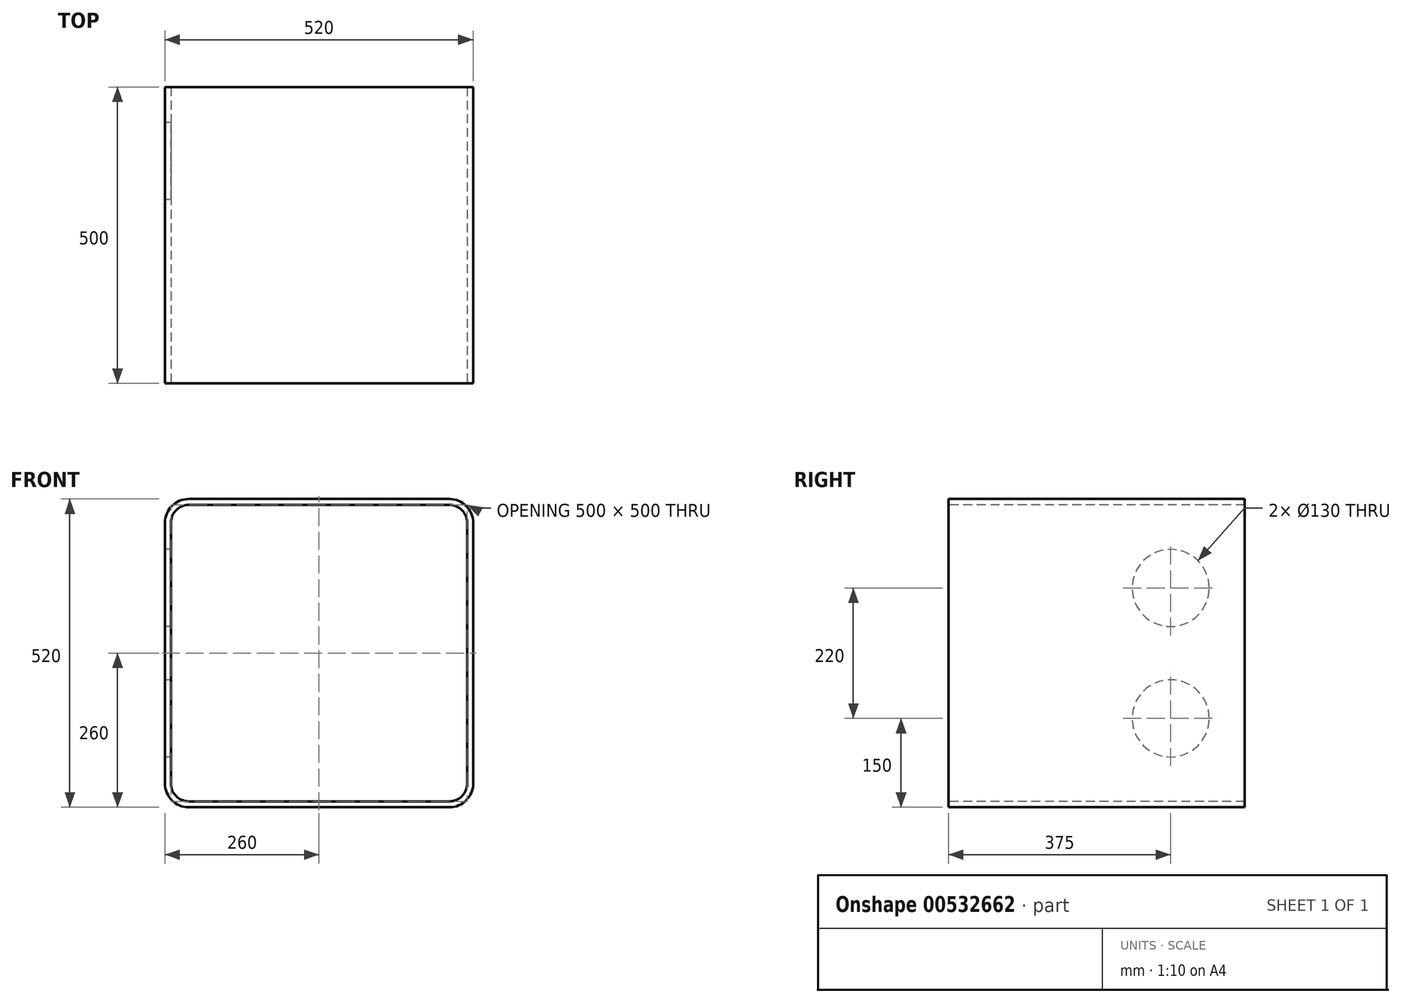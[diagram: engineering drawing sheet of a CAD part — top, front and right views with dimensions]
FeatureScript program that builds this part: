
annotation { "Feature Type Name" : "Feature", "Feature Type Description" : "" }
export const myFeature = defineFeature(function(context is Context, id is Id, definition is map)
    precondition{}
    {
        {
            var Q0;
            Q0=qCreatedBy(makeId("Front.planeOp"),FACE);
            var sketch = newSketch(context, id + "F0", { "sketchPlane" : qUnion([Q0])});
            skLineSegment(sketch, "E0.bottom", {"start": v(-215, 250) * mm, "end": v(225, 250) * mm});
            skLineSegment(sketch, "E0.top", {"start": v(-215, -250) * mm, "end": v(225, -250) * mm});
            skLineSegment(sketch, "E0.left", {"start": v(-245, 220) * mm, "end": v(-245, -220) * mm});
            skLineSegment(sketch, "E0.right", {"start": v(255, 220) * mm, "end": v(255, -220) * mm});
            skPoint(sketch, "E0.middle", {"position": v(0, 0) * mm});
            skPoint(sketch, "E1.visualSharp", {"position": v(-245, 250) * mm});
            skArc(sketch, "E1.filletArc", {"start": v(-215, 250) * mm, "mid": v(-236.21, 241.21) * mm, "end": v(-245, 220) * mm});
            skArc(sketch, "E2.filletArc", {"start": v(255, 220) * mm, "mid": v(246.21, 241.21) * mm, "end": v(225, 250) * mm});
            skArc(sketch, "E3.filletArc", {"start": v(225, -250) * mm, "mid": v(246.21, -241.21) * mm, "end": v(255, -220) * mm});
            skArc(sketch, "E4.filletArc", {"start": v(-245, -220) * mm, "mid": v(-236.21, -241.21) * mm, "end": v(-215, -250) * mm});
            skArc(sketch, "E5.0", {"start": v(-215, 260) * mm, "mid": v(-243.28, 248.28) * mm, "end": v(-255, 220) * mm});
            skLineSegment(sketch, "E5.1", {"start": v(-215, 260) * mm, "end": v(225, 260) * mm});
            skLineSegment(sketch, "E5.2", {"start": v(-255, 220) * mm, "end": v(-255, -220) * mm});
            skArc(sketch, "E5.3", {"start": v(265, 220) * mm, "mid": v(253.28, 248.28) * mm, "end": v(225, 260) * mm});
            skArc(sketch, "E5.4", {"start": v(-255, -220) * mm, "mid": v(-243.28, -248.28) * mm, "end": v(-215, -260) * mm});
            skLineSegment(sketch, "E5.5", {"start": v(-215, -260) * mm, "end": v(225, -260) * mm});
            skArc(sketch, "E5.6", {"start": v(225, -260) * mm, "mid": v(253.28, -248.28) * mm, "end": v(265, -220) * mm});
            skLineSegment(sketch, "E5.7", {"start": v(265, 220) * mm, "end": v(265, -220) * mm});
            skSolve(sketch);
        }
        {
            var Q0;
            Q0 = qSketchRegion(id + "F0", true);
            extrude(context, id + "F1", {"entities" : qUnion([Q0]), "oppositeDirection" : true, "depth" : 500 * mm, "offsetDistance" : 25 * mm});
        }
        {
            var Q0;
            Q0=makeQuery(id+"F1.opExtrude","SWEPT_FACE",FACE,{"disambiguationData":[OSD([sQuery(id+"F0.wireOp",EDGE,"E5.2")])]});
            var sketch = newSketch(context, id + "F2", { "sketchPlane" : qUnion([Q0])});
            skCircle(sketch, "E6", {"center": v(-375, 110) * mm, "radius": 65 * mm});
            skCircle(sketch, "E7", {"center": v(-375, -110) * mm, "radius": 65 * mm});
            skSolve(sketch);
        }
        {
            var Q0;
            Q0=makeQuery(id+"F2.imprint","IMPRINT",FACE,{"disambiguationData":[TD([[makeQuery(id+"F2.imprint","IMPRINT",EDGE,{"derivedFrom":sQuery(id+"F2.wireOp",EDGE,"E6")}),1.0]])]});
            var Q1;
            Q1=makeQuery(id+"F2.imprint","IMPRINT",FACE,{"disambiguationData":[TD([[makeQuery(id+"F2.imprint","IMPRINT",EDGE,{"derivedFrom":sQuery(id+"F2.wireOp",EDGE,"E7")}),1.0]])]});
            extrude(context, id + "F3", {"entities" : qUnion([Q0, Q1]), "operationType" : NewBodyOperationType.REMOVE, "oppositeDirection" : true, "depth" : 25 * mm, "offsetDistance" : 25 * mm});
        }
    });
